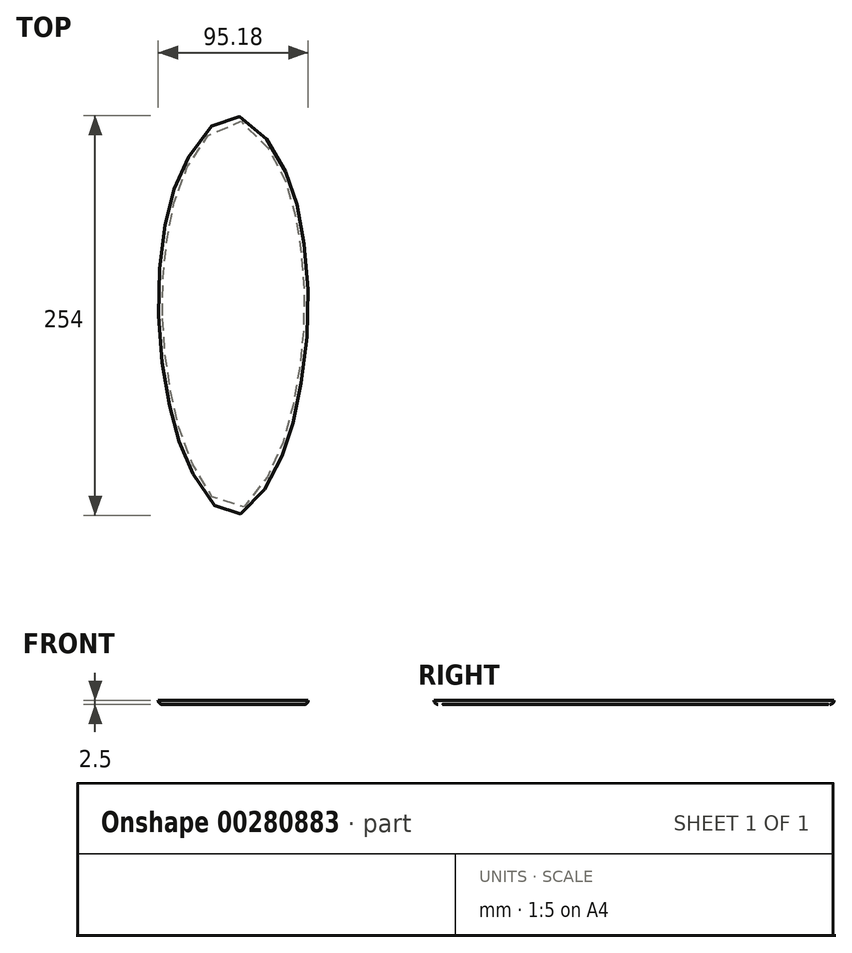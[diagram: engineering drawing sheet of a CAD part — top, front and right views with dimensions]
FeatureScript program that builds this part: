
annotation { "Feature Type Name" : "Feature", "Feature Type Description" : "" }
export const myFeature = defineFeature(function(context is Context, id is Id, definition is map)
    precondition{}
    {
        {
            var Q0;
            Q0=qCreatedBy(makeId("Top.planeOp"),FACE);
            var sketch = newSketch(context, id + "F0", { "sketchPlane" : qUnion([Q0])});
            skLineSegment(sketch, "E0", {"start": v(0, 0) * mm, "end": v(0, 63.5) * mm, "construction": true});
            skLineSegment(sketch, "E1", {"start": v(0, 63.5) * mm, "end": v(0, 101.6) * mm, "construction": true});
            skLineSegment(sketch, "E2", {"start": v(0, 101.6) * mm, "end": v(0, 127) * mm, "construction": true});
            skLineSegment(sketch, "E3.MirrorCS", {"start": v(0, 0) * mm, "end": v(0, -63.5) * mm, "construction": true});
            skLineSegment(sketch, "E4.MirrorCS", {"start": v(0, -63.5) * mm, "end": v(0, -101.6) * mm, "construction": true});
            skLineSegment(sketch, "E5.MirrorCS", {"start": v(0, -101.6) * mm, "end": v(0, -127) * mm, "construction": true});
            skLineSegment(sketch, "E6", {"start": v(0, 0) * mm, "end": v(47.5, 0) * mm, "construction": true});
            skLineSegment(sketch, "E7", {"start": v(0, 63.5) * mm, "end": v(42, 63.5) * mm, "construction": true});
            skLineSegment(sketch, "E8", {"start": v(0, 101.6) * mm, "end": v(28, 101.6) * mm, "construction": true});
            skLineSegment(sketch, "E9", {"start": v(0, -63.5) * mm, "end": v(39, -63.5) * mm, "construction": true});
            skLineSegment(sketch, "E10", {"start": v(0, -101.6) * mm, "end": v(25, -101.6) * mm, "construction": true});
            skLineSegment(sketch, "E11.MirrorCS", {"start": v(0, 101.6) * mm, "end": v(-28, 101.6) * mm, "construction": true});
            skLineSegment(sketch, "E12.MirrorCS", {"start": v(0, 63.5) * mm, "end": v(-42, 63.5) * mm, "construction": true});
            skLineSegment(sketch, "E13.MirrorCS", {"start": v(0, 0) * mm, "end": v(-47.5, 0) * mm, "construction": true});
            skLineSegment(sketch, "E14.MirrorCS", {"start": v(0, -63.5) * mm, "end": v(-39, -63.5) * mm, "construction": true});
            skLineSegment(sketch, "E15.MirrorCS", {"start": v(0, -101.6) * mm, "end": v(-25, -101.6) * mm, "construction": true});
            skFitSpline(sketch, "E16", {"points": [v(-47.5, 0) * mm, v(-42, 63.5) * mm, v(-28, 101.6) * mm, v(0, 127) * mm, v(28, 101.6) * mm, v(42, 63.5) * mm, v(47.5, 0) * mm, v(39, -63.5) * mm, v(25, -101.6) * mm, v(0, -127) * mm, v(-25, -101.6) * mm, v(-39, -63.5) * mm, v(-47.5, 0) * mm]});
            skSolve(sketch);
        }
        {
            var Q0;
            Q0 = qSketchRegion(id + "F0", true);
            extrude(context, id + "F1", {"entities" : qUnion([Q0]), "depth" : 2.5 * mm});
        }
        {
            var Q0;
            Q0=makeQuery(id+"F1.opExtrude","CAP_EDGE",EDGE,{"disambiguationData":[OSD([sQuery(id+"F0.wireOp",EDGE,"E16")])],"isStart":true});
            fillet(context, id + "F2", {"entities" : qUnion([Q0]), "radius" : 2.5 * mm, "tangentPropagation" : true, "allowEdgeOverflow" : false});
        }
    });
